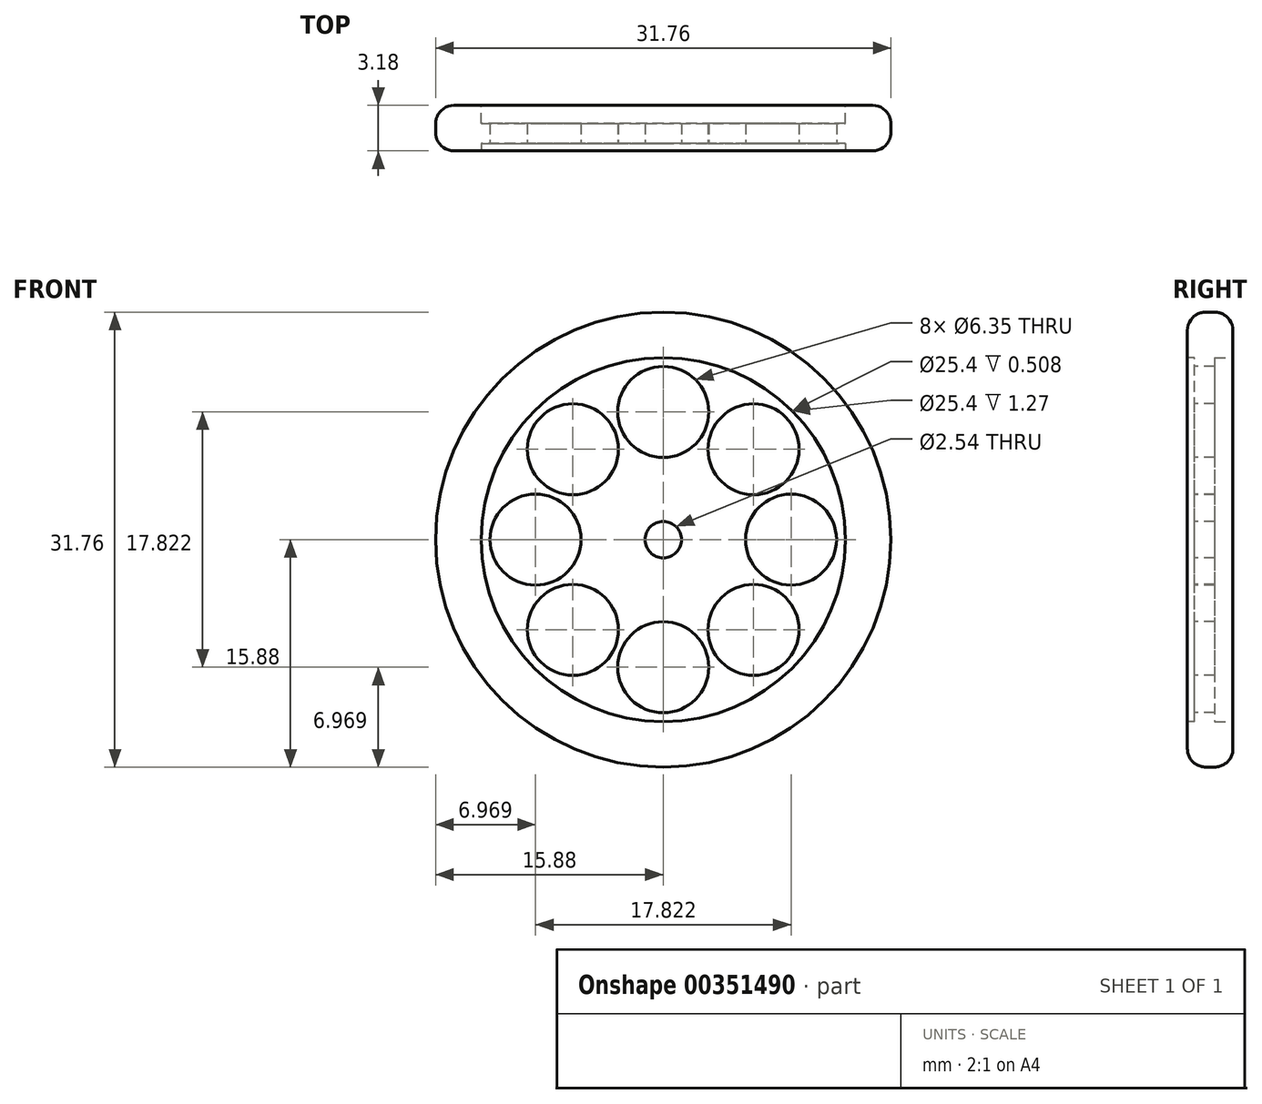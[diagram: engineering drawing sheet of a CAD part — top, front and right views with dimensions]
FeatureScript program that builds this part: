
annotation { "Feature Type Name" : "Feature", "Feature Type Description" : "" }
export const myFeature = defineFeature(function(context is Context, id is Id, definition is map)
    precondition{}
    {
        {
            var Q0;
            Q0=qCreatedBy(makeId("Front.planeOp"),FACE);
            var sketch = newSketch(context, id + "F0", { "sketchPlane" : qUnion([Q0])});
            skCircle(sketch, "E0", {"center": v(0, 0) * mm, "radius": 15.88 * mm});
            skSolve(sketch);
        }
        {
            var Q0;
            Q0 = qSketchRegion(id + "F0", true);
            extrude(context, id + "F1", {"entities" : qUnion([Q0]), "depth" : 3.17 * mm, "symmetric" : true});
        }
        {
            var Q0;
            Q0=makeQuery(id+"F1.opExtrude","CAP_FACE",FACE,{"disambiguationData":[OSD([sQuery(id+"F0.wireOp",EDGE,"E0")])],"isStart":false});
            var sketch = newSketch(context, id + "F2", { "sketchPlane" : qUnion([Q0])});
            skCircle(sketch, "E1", {"center": v(0, 0) * mm, "radius": 12.7 * mm});
            skSolve(sketch);
        }
        {
            var Q0;
            Q0 = qSketchRegion(id + "F2", true);
            extrude(context, id + "F3", {"entities" : qUnion([Q0]), "operationType" : NewBodyOperationType.REMOVE, "oppositeDirection" : true, "depth" : 0.5 * mm});
        }
        {
            var Q0;
            Q0=makeQuery(id+"F1.opExtrude","CAP_FACE",FACE,{"disambiguationData":[OSD([sQuery(id+"F0.wireOp",EDGE,"E0")])],"isStart":true});
            var sketch = newSketch(context, id + "F4", { "sketchPlane" : qUnion([Q0])});
            skCircle(sketch, "E2", {"center": v(0, 0) * mm, "radius": 12.7 * mm});
            skSolve(sketch);
        }
        {
            var Q0;
            Q0 = qSketchRegion(id + "F4", true);
            extrude(context, id + "F5", {"entities" : qUnion([Q0]), "operationType" : NewBodyOperationType.REMOVE, "oppositeDirection" : true, "depth" : 1.27 * mm});
        }
        {
            var Q0;
            Q0=makeQuery(id+"F3.boolean.opBoolean","COPY",FACE,{"derivedFrom":makeQuery(id+"F3.opExtrude","CAP_FACE",FACE,{"disambiguationData":[OSD([sQuery(id+"F2.wireOp",EDGE,"E1")])],"isStart":false})});
            var sketch = newSketch(context, id + "F6", { "sketchPlane" : qUnion([Q0])});
            skCircle(sketch, "E3", {"center": v(0, 0) * mm, "radius": 1.27 * mm});
            skSolve(sketch);
        }
        {
            var Q0;
            Q0 = qSketchRegion(id + "F6", true);
            extrude(context, id + "F7", {"entities" : qUnion([Q0]), "operationType" : NewBodyOperationType.REMOVE, "endBound" : BoundingType.THROUGH_ALL, "oppositeDirection" : true, "depth" : 25.4 * mm});
        }
        {
            var Q0;
            Q0=makeQuery(id+"F3.boolean.opBoolean","COPY",FACE,{"derivedFrom":makeQuery(id+"F3.opExtrude","CAP_FACE",FACE,{"disambiguationData":[OSD([sQuery(id+"F2.wireOp",EDGE,"E1")])],"isStart":false})});
            var sketch = newSketch(context, id + "F8", { "sketchPlane" : qUnion([Q0])});
            skCircle(sketch, "E4", {"center": v(0, 8.91) * mm, "radius": 3.18 * mm});
            skCircle(sketch, "E5.1.0", {"center": v(-6.3, 6.3) * mm, "radius": 3.18 * mm});
            skCircle(sketch, "E5.2.0", {"center": v(-8.91, 0) * mm, "radius": 3.18 * mm});
            skCircle(sketch, "E5.3.0", {"center": v(-6.3, -6.3) * mm, "radius": 3.18 * mm});
            skCircle(sketch, "E5.4.0", {"center": v(0, -8.91) * mm, "radius": 3.18 * mm});
            skCircle(sketch, "E5.5.0", {"center": v(6.3, -6.3) * mm, "radius": 3.18 * mm});
            skCircle(sketch, "E5.6.0", {"center": v(8.91, 0) * mm, "radius": 3.18 * mm});
            skCircle(sketch, "E5.7.0", {"center": v(6.3, 6.3) * mm, "radius": 3.18 * mm});
            skPoint(sketch, "E5.center", {"position": v(0, 0) * mm});
            skSolve(sketch);
        }
        {
            var Q0;
            Q0 = qSketchRegion(id + "F8", true);
            extrude(context, id + "F9", {"entities" : qUnion([Q0]), "operationType" : NewBodyOperationType.REMOVE, "endBound" : BoundingType.THROUGH_ALL, "oppositeDirection" : true, "depth" : 25.4 * mm});
        }
        {
            var Q0;
            Q0=makeQuery(id+"F1.opExtrude","CAP_EDGE",EDGE,{"disambiguationData":[OSD([sQuery(id+"F0.wireOp",EDGE,"E0")])],"isStart":false});
            var Q1;
            Q1=makeQuery(id+"F1.opExtrude","SWEPT_FACE",FACE,{"disambiguationData":[OSD([sQuery(id+"F0.wireOp",EDGE,"E0")])]});
            fillet(context, id + "F10", {"entities" : qUnion([Q0, Q1]), "radius" : 1.27 * mm, "tangentPropagation" : true, "allowEdgeOverflow" : false});
        }
    });
